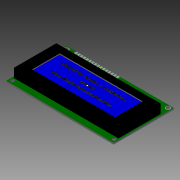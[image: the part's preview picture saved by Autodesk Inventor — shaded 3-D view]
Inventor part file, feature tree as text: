
AUTODESK INVENTOR PART (.ipt)
format: ipt  version: 2015 (Build 190159000, 159)  size: 364,544 bytes
history: native  units: in
note: dims shown in document units (in); Inventor stores cm internally (conversion verified against a paired STEP export)
features: imported_body x4, other x3, sketch x2, extrude x1, plane x1, fillet x1, mirror x1
ambient origin geometry x8: Origin, YZ Plane, XZ Plane, XY Plane, X Axis, Y Axis, Z Axis, Center Point
bodies: Body1 (feature_tree), Body2 (feature_tree), Body3 (feature_tree), Body4 (feature_tree)
feature tree (13):
  other  "20X4LCD JHD204A1"
  extrude  "Extrusion1"  Depth=0.1693in
  plane  "Work Plane1"
  sketch  "Sketch2"  dims[d4=0.3937in d5=0.0in d6=0.3125in]
  other  "Boss-Extrude2[3]"
  other  "Boss-Extrude2[4]"
  fillet  "Fillet1"  Radius=0.1299in
  mirror  "Mirror1"
  imported_body  "Base3"
  imported_body  "Base4"
  imported_body  "Base5"
  imported_body  "Base6"
  sketch  "Sketch1"  dims[d0=0.1299in d1=0.1693in d2=0.1299in d3=0.1693in]
